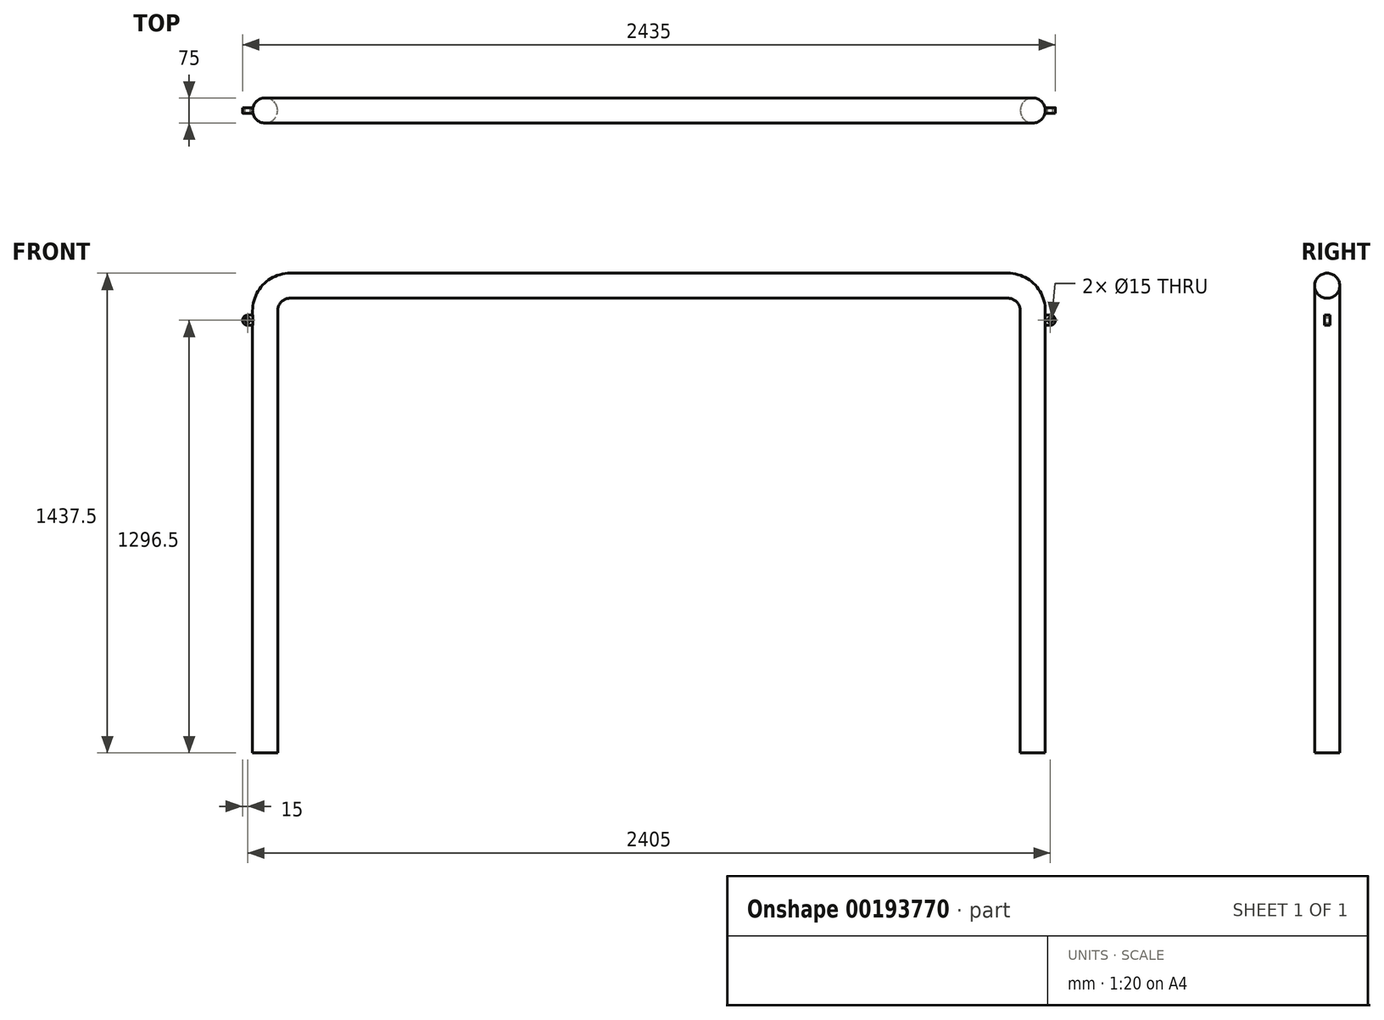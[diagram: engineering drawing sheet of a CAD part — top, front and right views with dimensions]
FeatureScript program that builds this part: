
annotation { "Feature Type Name" : "Feature", "Feature Type Description" : "" }
export const myFeature = defineFeature(function(context is Context, id is Id, definition is map)
    precondition{}
    {
        {
            var Q0;
            Q0=qCreatedBy(makeId("Top.planeOp"),FACE);
            var sketch = newSketch(context, id + "F0", { "sketchPlane" : qUnion([Q0])});
            skCircle(sketch, "E0", {"center": v(-1150, 0) * mm, "radius": 42.68 * mm});
            skCircle(sketch, "E1", {"center": v(1150, 0) * mm, "radius": 37.5 * mm});
            skLineSegment(sketch, "E2", {"start": v(0, 0) * mm, "end": v(0, 1195.95) * mm, "construction": true});
            skSolve(sketch);
        }
        {
            var Q0;
            Q0=qCreatedBy(makeId("Front.planeOp"),FACE);
            var sketch = newSketch(context, id + "F1", { "sketchPlane" : qUnion([Q0])});
            skLineSegment(sketch, "E3", {"start": v(-1150, 0) * mm, "end": v(-1150, 1325) * mm});
            skLineSegment(sketch, "E4", {"start": v(-1075, 1400) * mm, "end": v(1075, 1400) * mm});
            skLineSegment(sketch, "E5", {"start": v(1150, 1325) * mm, "end": v(1150, 0) * mm});
            skPoint(sketch, "E6.visualSharp", {"position": v(-1150, 1400) * mm});
            skArc(sketch, "E6.filletArc", {"start": v(-1075, 1400) * mm, "mid": v(-1128.03, 1378.03) * mm, "end": v(-1150, 1325) * mm});
            skPoint(sketch, "E7.visualSharp", {"position": v(1150, 1400) * mm});
            skArc(sketch, "E7.filletArc", {"start": v(1150, 1325) * mm, "mid": v(1128.03, 1378.03) * mm, "end": v(1075, 1400) * mm});
            skLineSegment(sketch, "E8", {"start": v(0, 0) * mm, "end": v(0, 2937.03) * mm, "construction": true});
            skSolve(sketch);
        }
        {
            var Q0;
            Q0=makeQuery(id+"F0.imprint","IMPRINT",FACE,{"disambiguationData":[TD([[makeQuery(id+"F0.imprint","IMPRINT",EDGE,{"derivedFrom":sQuery(id+"F0.wireOp",EDGE,"E1")}),1.0]])]});
            var Q1;
            Q1=sQuery(id+"F1.wireOp",EDGE,"E3");
            var Q2;
            Q2=sQuery(id+"F1.wireOp",EDGE,"E6.filletArc");
            var Q3;
            Q3=sQuery(id+"F1.wireOp",EDGE,"E4");
            var Q4;
            Q4=sQuery(id+"F1.wireOp",EDGE,"E7.filletArc");
            var Q5;
            Q5=sQuery(id+"F1.wireOp",EDGE,"E5");
            sweep(context, id + "F2", {"profiles" : qUnion([Q0]), "path" : qUnion([Q1, Q2, Q3, Q4, Q5])});
        }
        {
            var Q0;
            Q0=qCreatedBy(makeId("Front.planeOp"),FACE);
            var sketch = newSketch(context, id + "F3", { "sketchPlane" : qUnion([Q0])});
            skLineSegment(sketch, "E9.bottom", {"start": v(1150, 1311.5) * mm, "end": v(1202.5, 1311.5) * mm});
            skLineSegment(sketch, "E9.top", {"start": v(1150, 1281.5) * mm, "end": v(1202.5, 1281.5) * mm});
            skLineSegment(sketch, "E9.left", {"start": v(1150, 1311.5) * mm, "end": v(1150, 1281.5) * mm});
            skLineSegment(sketch, "E9.right", {"start": v(1217.5, 1296.5) * mm, "end": v(1217.5, 1296.5) * mm});
            skLineSegment(sketch, "E10", {"start": v(-1371.73, 0) * mm, "end": v(1582.2, 0) * mm, "construction": true});
            skLineSegment(sketch, "E11", {"start": v(1150, 1681.63) * mm, "end": v(1150, -220.36) * mm, "construction": true});
            skLineSegment(sketch, "E12", {"start": v(0, 0) * mm, "end": v(0, 2261.52) * mm, "construction": true});
            skLineSegment(sketch, "E13.MirrorCS", {"start": v(-1150, 1681.63) * mm, "end": v(-1150, -220.36) * mm, "construction": true});
            skLineSegment(sketch, "E14", {"start": v(-1401.94, 1296.5) * mm, "end": v(2101.58, 1296.5) * mm, "construction": true});
            skLineSegment(sketch, "E15", {"start": v(-1150, 1311.5) * mm, "end": v(-1150, 1281.5) * mm});
            skCircle(sketch, "E16", {"center": v(1202.5, 1296.5) * mm, "radius": 7.5 * mm});
            skPoint(sketch, "E17.visualSharp", {"position": v(1217.5, 1311.5) * mm});
            skArc(sketch, "E17.filletArc", {"start": v(1217.5, 1296.5) * mm, "mid": v(1213.1, 1307.1) * mm, "end": v(1202.5, 1311.5) * mm});
            skPoint(sketch, "E18.visualSharp", {"position": v(1217.5, 1281.5) * mm});
            skArc(sketch, "E18.filletArc", {"start": v(1202.5, 1281.5) * mm, "mid": v(1213.1, 1285.9) * mm, "end": v(1217.5, 1296.5) * mm});
            skLineSegment(sketch, "E19.MirrorCS", {"start": v(-1150, 1311.5) * mm, "end": v(-1202.5, 1311.5) * mm});
            skArc(sketch, "E20.MirrorCS", {"start": v(-1217.5, 1296.5) * mm, "mid": v(-1213.1, 1307.1) * mm, "end": v(-1202.5, 1311.5) * mm});
            skArc(sketch, "E21.MirrorCS", {"start": v(-1202.5, 1281.5) * mm, "mid": v(-1213.1, 1285.9) * mm, "end": v(-1217.5, 1296.5) * mm});
            skLineSegment(sketch, "E22.MirrorCS", {"start": v(-1150, 1281.5) * mm, "end": v(-1202.5, 1281.5) * mm});
            skCircle(sketch, "E23.MirrorC", {"center": v(-1202.5, 1296.5) * mm, "radius": 7.5 * mm});
            skSolve(sketch);
        }
        {
            var Q0;
            Q0 = qSketchRegion(id + "F3", true);
            extrude(context, id + "F4", {"entities" : qUnion([Q0]), "operationType" : NewBodyOperationType.ADD, "depth" : 8.33 * mm, "hasSecondDirection" : true, "secondDirectionOppositeDirection" : true, "secondDirectionDepth" : 8.33 * mm});
        }
    });
